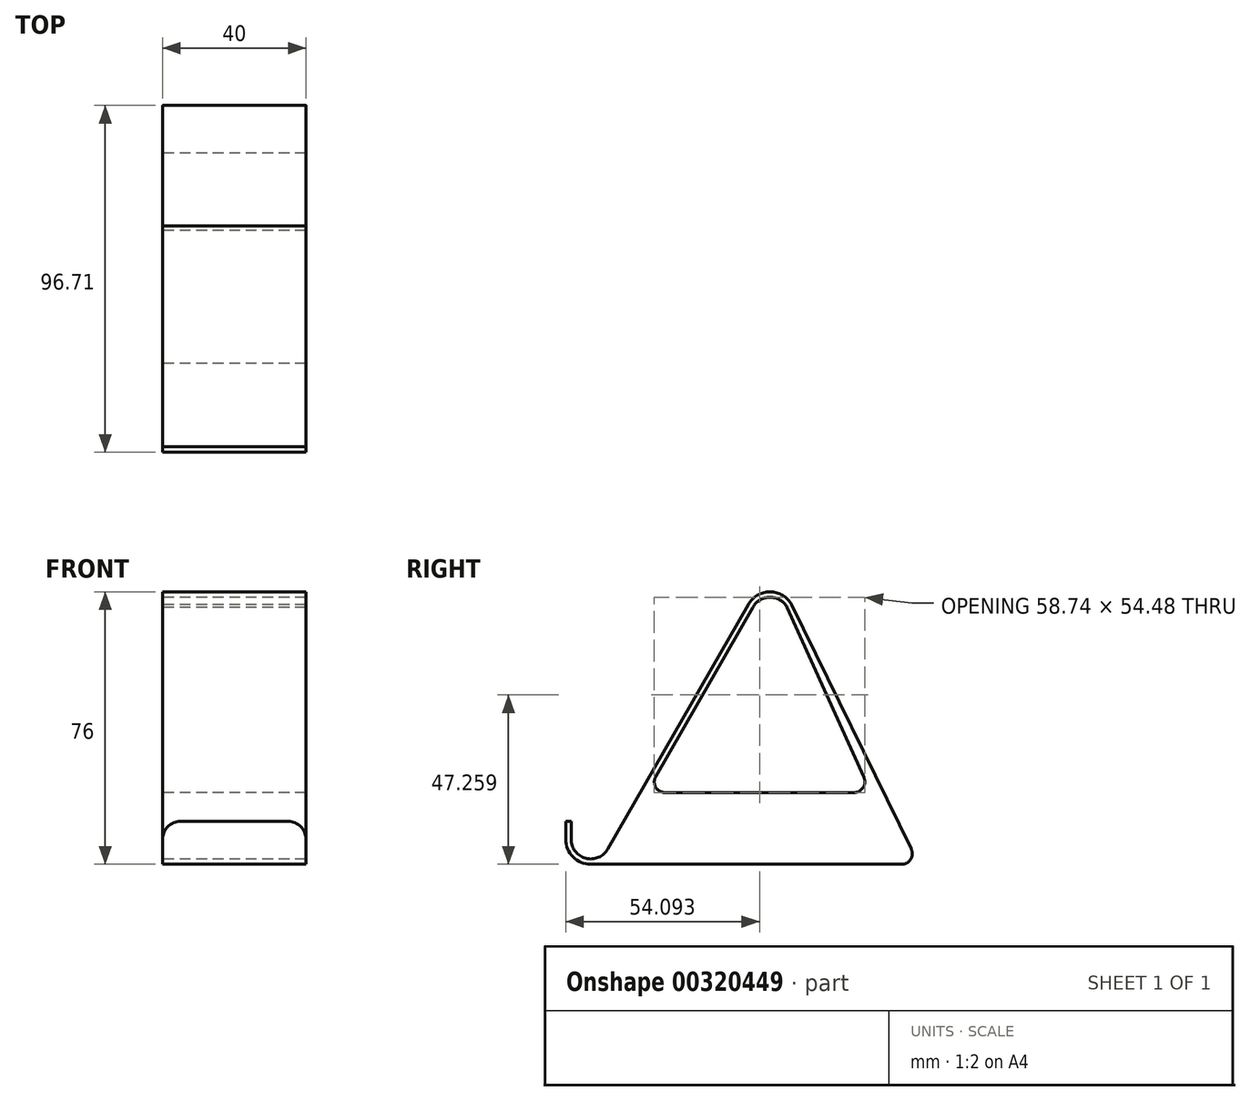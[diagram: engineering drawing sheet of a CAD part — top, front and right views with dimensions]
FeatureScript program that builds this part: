
annotation { "Feature Type Name" : "Feature", "Feature Type Description" : "" }
export const myFeature = defineFeature(function(context is Context, id is Id, definition is map)
    precondition{}
    {
        {
            var Q0;
            Q0=qCreatedBy(makeId("Right.planeOp"),FACE);
            var sketch = newSketch(context, id + "F0", { "sketchPlane" : qUnion([Q0])});
            skArc(sketch, "E0", {"start": v(-7, 0) * mm, "mid": v(-4.95, -4.95) * mm, "end": v(0, -7) * mm});
            skArc(sketch, "E1", {"start": v(54.77, 64.74) * mm, "mid": v(50, 67.5) * mm, "end": v(45.23, 64.74) * mm});
            skLineSegment(sketch, "E2", {"start": v(18.12, 17.51) * mm, "end": v(45.23, 64.74) * mm});
            skLineSegment(sketch, "E3", {"start": v(50, 62) * mm, "end": v(50, -44.3) * mm, "construction": true});
            skLineSegment(sketch, "E4", {"start": v(0, -7) * mm, "end": v(86.7, -7) * mm, "construction": true});
            skPoint(sketch, "E5.orphan", {"position": v(93.93, -3.48) * mm});
            skLineSegment(sketch, "E6", {"start": v(-7, 0) * mm, "end": v(-7, 5) * mm});
            skLineSegment(sketch, "E7.0", {"start": v(-5.5, 0) * mm, "end": v(-5.5, 5) * mm});
            skLineSegment(sketch, "E7.1", {"start": v(89.4, -2.68) * mm, "end": v(56.07, 65.48) * mm});
            skArc(sketch, "E7.2", {"start": v(56.07, 65.48) * mm, "mid": v(50, 69) * mm, "end": v(43.93, 65.48) * mm});
            skLineSegment(sketch, "E7.3", {"start": v(4.77, -2.74) * mm, "end": v(43.93, 65.48) * mm});
            skArc(sketch, "E7.4", {"start": v(-5.5, 0) * mm, "mid": v(-1.42, -5.31) * mm, "end": v(4.77, -2.74) * mm});
            skLineSegment(sketch, "E8", {"start": v(-5.5, 5) * mm, "end": v(-7, 5) * mm});
            skLineSegment(sketch, "E9", {"start": v(0, -7) * mm, "end": v(97.68, -7) * mm});
            skLineSegment(sketch, "E10.trimOffspring", {"start": v(20.72, 13.02) * mm, "end": v(73.47, 13.02) * mm});
            skLineSegment(sketch, "E11.trimOffspring", {"start": v(76.2, 17.25) * mm, "end": v(54.77, 64.74) * mm});
            skPoint(sketch, "E12.orphan", {"position": v(6.07, -3.48) * mm});
            skPoint(sketch, "E13.visualSharp", {"position": v(15.54, 13.02) * mm});
            skArc(sketch, "E13.filletArc", {"start": v(18.12, 17.51) * mm, "mid": v(18.13, 14.51) * mm, "end": v(20.72, 13.02) * mm});
            skPoint(sketch, "E14.visualSharp", {"position": v(78.12, 13.02) * mm});
            skArc(sketch, "E14.filletArc", {"start": v(73.47, 13.02) * mm, "mid": v(75.99, 14.4) * mm, "end": v(76.2, 17.25) * mm});
            skArc(sketch, "E15.filletArc", {"start": v(86.7, -7) * mm, "mid": v(89.25, -5.59) * mm, "end": v(89.4, -2.68) * mm});
            skSolve(sketch);
        }
        {
            var Q0;
            {var subQ0=sQuery(id+"F0.wireOp",EDGE,"E0");Q0=makeQuery(id+"F0.imprint","IMPRINT",FACE,{"disambiguationData":[TD([[makeQuery(id+"F0.imprint","IMPRINT",EDGE,{"derivedFrom":subQ0}),1.0]])]});}
            extrude(context, id + "F1", {"entities" : qUnion([Q0]), "depth" : 40 * mm});
        }
        {
            var Q0;
            Q0=makeQuery(id+"F1.opExtrude","CAP_EDGE",EDGE,{"disambiguationData":[OSD([sQuery(id+"F0.wireOp",EDGE,"E8")])],"isStart":false});
            var Q1;
            Q1=makeQuery(id+"F1.opExtrude","CAP_EDGE",EDGE,{"disambiguationData":[OSD([sQuery(id+"F0.wireOp",EDGE,"E8")])],"isStart":true});
            fillet(context, id + "F2", {"entities" : qUnion([Q0, Q1]), "radius" : 5 * mm, "tangentPropagation" : true, "allowEdgeOverflow" : false});
        }
    });
